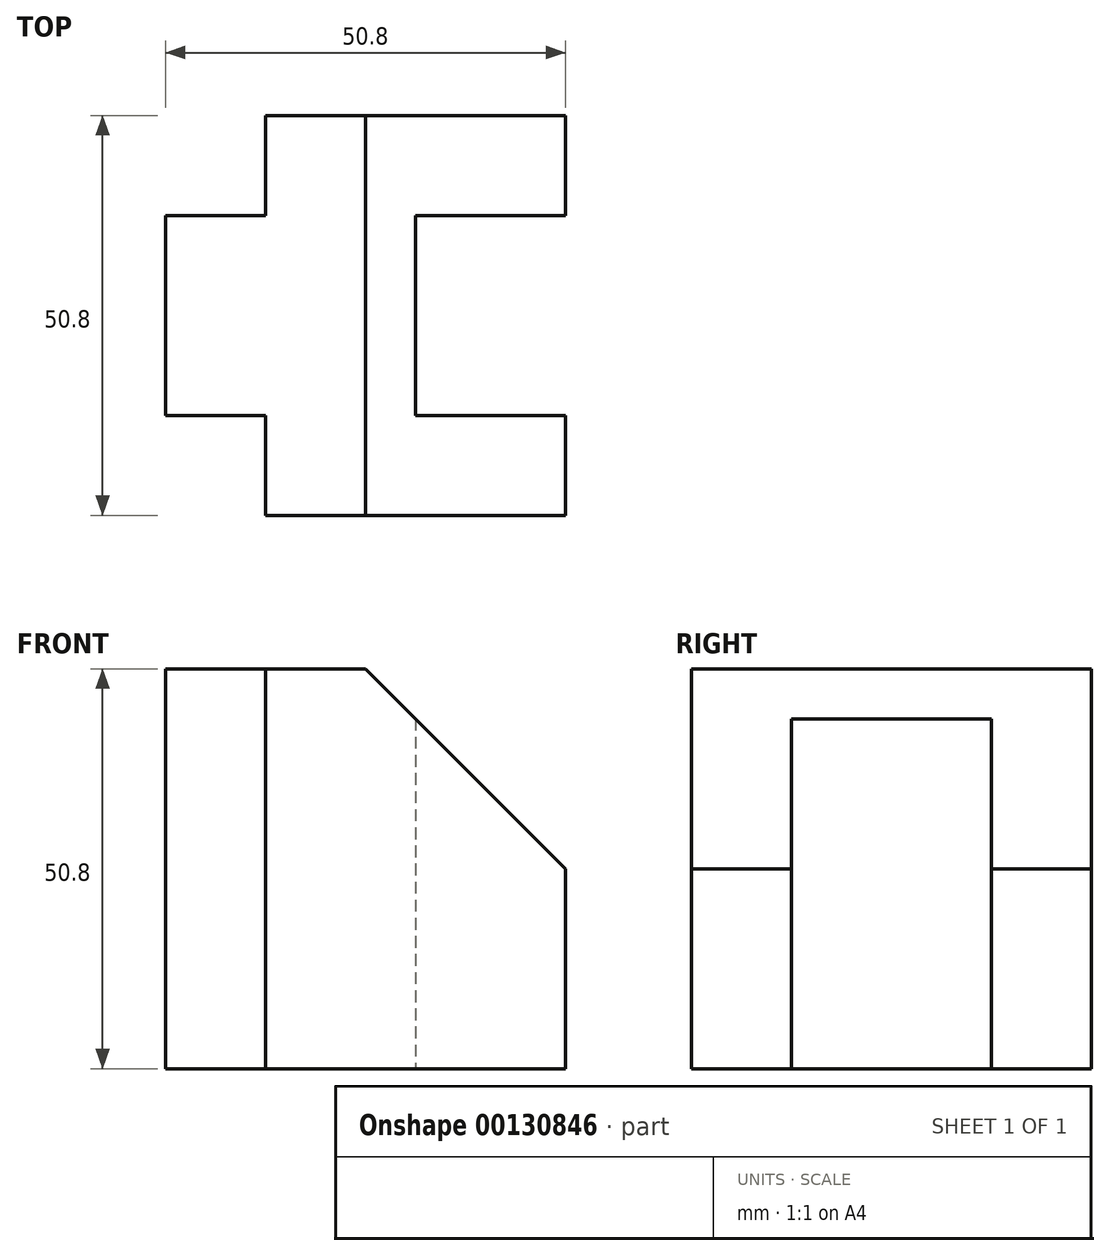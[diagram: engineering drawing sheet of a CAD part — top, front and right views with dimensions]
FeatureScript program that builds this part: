
annotation { "Feature Type Name" : "Feature", "Feature Type Description" : "" }
export const myFeature = defineFeature(function(context is Context, id is Id, definition is map)
    precondition{}
    {
        {
            var Q0;
            Q0=qCreatedBy(makeId("Top.planeOp"),FACE);
            var sketch = newSketch(context, id + "F0", { "sketchPlane" : qUnion([Q0])});
            skLineSegment(sketch, "E0.bottom", {"start": v(0, 0) * mm, "end": v(50.8, 0) * mm});
            skLineSegment(sketch, "E0.top", {"start": v(0, 50.8) * mm, "end": v(50.8, 50.8) * mm});
            skLineSegment(sketch, "E0.left", {"start": v(0, 0) * mm, "end": v(0, 50.8) * mm});
            skLineSegment(sketch, "E0.right", {"start": v(50.8, 0) * mm, "end": v(50.8, 50.8) * mm});
            skSolve(sketch);
        }
        {
            var Q0;
            Q0 = qSketchRegion(id + "F0", true);
            extrude(context, id + "F1", {"entities" : qUnion([Q0]), "depth" : 50.8 * mm});
        }
        {
            var Q0;
            Q0=qCreatedBy(makeId("Top.planeOp"),FACE);
            var sketch = newSketch(context, id + "F2", { "sketchPlane" : qUnion([Q0])});
            skLineSegment(sketch, "E1.bottom", {"start": v(31.75, 38.1) * mm, "end": v(50.8, 38.1) * mm});
            skLineSegment(sketch, "E1.top", {"start": v(31.75, 12.7) * mm, "end": v(50.8, 12.7) * mm});
            skLineSegment(sketch, "E1.left", {"start": v(31.75, 38.1) * mm, "end": v(31.75, 12.7) * mm});
            skLineSegment(sketch, "E1.right", {"start": v(50.8, 38.1) * mm, "end": v(50.8, 12.7) * mm});
            skSolve(sketch);
        }
        {
            var Q0;
            Q0 = qSketchRegion(id + "F2", true);
            extrude(context, id + "F3", {"entities" : qUnion([Q0]), "operationType" : NewBodyOperationType.REMOVE, "depth" : 50.8 * mm});
        }
        {
            var Q0;
            Q0=qCreatedBy(makeId("Top.planeOp"),FACE);
            var sketch = newSketch(context, id + "F4", { "sketchPlane" : qUnion([Q0])});
            skLineSegment(sketch, "E2.bottom", {"start": v(0, 38.1) * mm, "end": v(12.7, 38.1) * mm});
            skLineSegment(sketch, "E2.top", {"start": v(0, 50.8) * mm, "end": v(12.7, 50.8) * mm});
            skLineSegment(sketch, "E2.left", {"start": v(0, 38.1) * mm, "end": v(0, 50.8) * mm});
            skLineSegment(sketch, "E2.right", {"start": v(12.7, 38.1) * mm, "end": v(12.7, 50.8) * mm});
            skLineSegment(sketch, "E3.bottom", {"start": v(0, 0) * mm, "end": v(12.7, 0) * mm});
            skLineSegment(sketch, "E3.top", {"start": v(0, 12.7) * mm, "end": v(12.7, 12.7) * mm});
            skLineSegment(sketch, "E3.left", {"start": v(0, 0) * mm, "end": v(0, 12.7) * mm});
            skLineSegment(sketch, "E3.right", {"start": v(12.7, 0) * mm, "end": v(12.7, 12.7) * mm});
            skSolve(sketch);
        }
        {
            var Q0;
            Q0 = qSketchRegion(id + "F4", true);
            extrude(context, id + "F5", {"entities" : qUnion([Q0]), "operationType" : NewBodyOperationType.REMOVE, "depth" : 50.8 * mm});
        }
        {
            var Q0;
            Q0=qCreatedBy(makeId("Front.planeOp"),FACE);
            var sketch = newSketch(context, id + "F6", { "sketchPlane" : qUnion([Q0])});
            skLineSegment(sketch, "E4", {"start": v(25.4, 50.8) * mm, "end": v(50.8, 50.8) * mm});
            skLineSegment(sketch, "E5", {"start": v(50.8, 50.8) * mm, "end": v(50.8, 25.4) * mm});
            skLineSegment(sketch, "E6", {"start": v(50.8, 25.4) * mm, "end": v(25.4, 50.8) * mm});
            skLineSegment(sketch, "E7", {"start": v(50.8, 25.4) * mm, "end": v(50.8, 50.8) * mm});
            skSolve(sketch);
        }
        {
            var Q0;
            Q0 = qSketchRegion(id + "F6", true);
            extrude(context, id + "F7", {"entities" : qUnion([Q0]), "operationType" : NewBodyOperationType.REMOVE, "oppositeDirection" : true, "depth" : 50.8 * mm});
        }
    });
